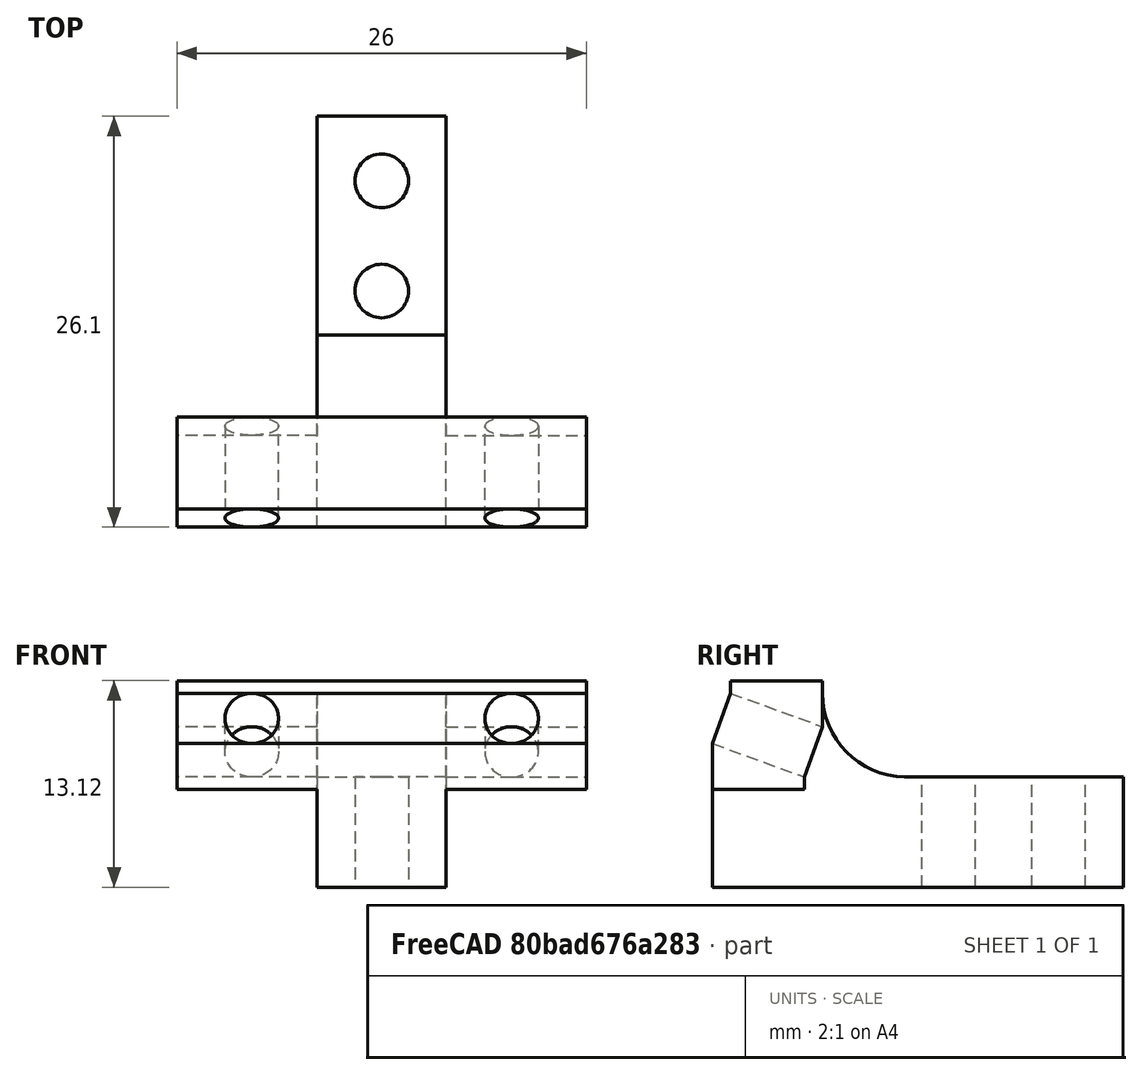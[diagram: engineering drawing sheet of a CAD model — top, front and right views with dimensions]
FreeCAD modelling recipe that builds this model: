
FCSTD DOCUMENT  (FreeCAD 0.19R24291 (Git))
Label: Иголки 70 2
License: All rights reserved
LicenseURL: http://en.wikipedia.org/wiki/All_rights_reserved
objects: PartDesign::Pad×5, Sketcher::SketchObject×4, Mesh::Feature×1, PartDesign::Pocket×1, PartDesign::Mirrored×1, PartDesign::Body×1
note: 18 computed .brp shape members not serialized (recipe doc carries the construction recipe); baked Part::Feature solids carry a one-line shape summary decoded from their .brp

FEATURE [Mesh::Feature] ____________55  label="Иголки55"
FEATURE [Sketcher::SketchObject] Sketch
  FullyConstrained = true
  MapMode = 5
  Support = -> [XY_Plane]
  sketch-geometry (8):
    g0: ArcOfCircle CenterX=0 CenterY=22 CenterZ=0 NormalX=0 NormalY=0 NormalZ=1 AngleXU=0 Radius=1.7 StartAngle=1.5708 EndAngle=4.71239
    g1: ArcOfCircle CenterX=0 CenterY=15 CenterZ=0 NormalX=0 NormalY=0 NormalZ=1 AngleXU=0 Radius=1.7 StartAngle=1.5708 EndAngle=4.71239
    g2: LineSegment StartX=1e-16 StartY=23.7 StartZ=0 EndX=0 EndY=26.1 EndZ=0
    g3: LineSegment StartX=0 StartY=26.1 StartZ=0 EndX=-4.1 EndY=26.1 EndZ=0
    g4: LineSegment StartX=-4.1 StartY=26.1 StartZ=0 EndX=-4.1 EndY=0 EndZ=0
    g5: LineSegment StartX=-4.1 StartY=0 StartZ=0 EndX=0 EndY=0 EndZ=0
    g6: LineSegment StartX=0 StartY=0 StartZ=0 EndX=-3e-16 EndY=13.3 EndZ=0
    g7: LineSegment StartX=1e-16 StartY=16.7 StartZ=0 EndX=-3e-16 EndY=20.3 EndZ=0
  constraints (26):
    c: PointOnObject(g0,g-2)
    c: PointOnObject(g0,g-2)
    c: PointOnObject(g0,g-2)
    c: PointOnObject(g1,g-2)
    c: PointOnObject(g1,g-2)
    c: PointOnObject(g1,g-2)
    c: Diameter(g1) = 3.4
    c: Equal(g1,g0)
    c: Distance(g1,g0) = 7
    c: Coincident(g2,g0)
    c: PointOnObject(g2,g-2)
    c: Distance(g2) = 2.4
    c: Coincident(g3,g2)
    c: Horizontal(g3)
    c: Distance(g1,g-1) = 15
    c: Distance(g3) = 4.1
    c: Coincident(g4,g3)
    c: PointOnObject(g4,g-1)
    c: Vertical(g4)
    c: Coincident(g5,g4)
    c: Coincident(g5,g-1)
    c: Coincident(g6,g5)
    c: Coincident(g6,g1)
    c: Coincident(g7,g1)
    c: Coincident(g7,g0)
    c: Distance(g4) = 26.1
FEATURE [PartDesign::Pad] Pad
  Direction = (1,1,1)
  Length = 7
  Length2 = 100
  Profile = -> Sketch
  Type = 0
FEATURE [Sketcher::SketchObject] Sketch001
  FullyConstrained = true
  MapMode = 5
  Placement = pos=(0,0,0) rot=(0.57735,0.57735,0.57735;2.0944rad)
  Support = -> [YZ_Plane]
  sketch-geometry (11):
    g0: LineSegment StartX=0 StartY=6.999 StartZ=0 EndX=5.83713 EndY=6.999 EndZ=0
    g1: LineSegment StartX=5.83713 StartY=6.999 StartZ=0 EndX=7 EndY=10.194 EndZ=0
    g2: LineSegment StartX=7 StartY=10.194 StartZ=0 EndX=7 EndY=12.3185 EndZ=0
    g3: LineSegment StartX=7 StartY=12.3185 StartZ=0 EndX=1.16287 EndY=12.3185 EndZ=0
    g4: LineSegment StartX=1.16287 StartY=12.3185 StartZ=0 EndX=0 EndY=9.12354 EndZ=0
    g5: LineSegment StartX=0 StartY=9.12354 StartZ=0 EndX=0 EndY=6.999 EndZ=0
    g6: LineSegment StartX=0 StartY=6.999 StartZ=0 EndX=7 EndY=6.999 EndZ=0
    g7: LineSegment StartX=7 StartY=6.999 StartZ=0 EndX=7 EndY=12.3185 EndZ=0
    g8: LineSegment StartX=0 StartY=6.999 StartZ=0 EndX=0 EndY=12.3185 EndZ=0
    g9: LineSegment StartX=0 StartY=12.3185 StartZ=0 EndX=7 EndY=12.3185 EndZ=0
    g10: LineSegment StartX=0 StartY=9.12354 StartZ=0 EndX=5.83713 EndY=6.999 EndZ=0
  constraints (30):
    c: PointOnObject(g0,g-2)
    c: Horizontal(g0)
    c: Coincident(g0,g1)
    c: Coincident(g1,g2)
    c: Vertical(g2)
    c: Coincident(g2,g3)
    c: Horizontal(g3)
    c: Coincident(g3,g4)
    c: PointOnObject(g4,g-2)
    c: Coincident(g4,g5)
    c: Coincident(g5,g0)
    c: Distance(g-1,g0) = 6.999
    c: Equal(g0,g3)
    c: Equal(g2,g5)
    c: DistanceX(g2) = 7
    c: Coincident(g6,g0)
    c: Horizontal(g6)
    c: Coincident(g7,g6)
    c: Coincident(g7,g2)
    c: Vertical(g7)
    c: Coincident(g8,g0)
    c: PointOnObject(g8,g-2)
    c: Coincident(g9,g8)
    c: Coincident(g9,g2)
    c: Horizontal(g9)
    c: Distance(g1) = 3.4
    c: Angle(g1,g6) = 1.91986
    c: Coincident(g10,g4)
    c: Coincident(g10,g0)
    c: Perpendicular(g10,g1)
FEATURE [PartDesign::Pad] Pad001
  BaseFeature = -> Pad
  Direction = (1,1,1)
  Length = 13
  Length2 = 100
  Profile = -> Sketch001
  Reversed = true
  Type = 0
FEATURE [Sketcher::SketchObject] Sketch002
  FullyConstrained = true
  MapMode = 5
  Placement = pos=(0,0,0) rot=(0.57735,0.57735,0.57735;2.0944rad)
  Support = -> [YZ_Plane]
  expr: Constraints[11] = Sketch001.Constraints[11]
  expr: Constraints[14] = Sketch001.Constraints[14]
  expr: Constraints[25] = Sketch001.Constraints[25]
  expr: Constraints[26] = Sketch001.Constraints[26]
  sketch-geometry (13):
    g0: LineSegment StartX=0 StartY=6.999 StartZ=0 EndX=5.83713 EndY=6.999 EndZ=0
    g1: LineSegment StartX=5.83713 StartY=6.999 StartZ=0 EndX=7 EndY=10.194 EndZ=0
    g2: LineSegment StartX=7 StartY=10.194 StartZ=0 EndX=7 EndY=12.3185 EndZ=0
    g3: LineSegment StartX=7 StartY=12.3185 StartZ=0 EndX=1.16287 EndY=12.3185 EndZ=0
    g4: LineSegment StartX=1.16287 StartY=12.3185 StartZ=0 EndX=0 EndY=9.12354 EndZ=0
    g5: LineSegment StartX=0 StartY=9.12354 StartZ=0 EndX=0 EndY=6.999 EndZ=0
    g6: LineSegment StartX=0 StartY=6.999 StartZ=0 EndX=7 EndY=6.999 EndZ=0
    g7: LineSegment StartX=7 StartY=6.999 StartZ=0 EndX=7 EndY=12.3185 EndZ=0
    g8: LineSegment StartX=0 StartY=6.999 StartZ=0 EndX=0 EndY=12.3185 EndZ=0
    g9: LineSegment StartX=0 StartY=12.3185 StartZ=0 EndX=7 EndY=12.3185 EndZ=0
    g10: LineSegment StartX=0 StartY=9.12354 StartZ=0 EndX=5.83713 EndY=6.999 EndZ=0
    g11: ArcOfCircle CenterX=12.3195 CenterY=12.3185 CenterZ=0 NormalX=0 NormalY=0 NormalZ=1 AngleXU=0 Radius=5.31949 StartAngle=3.14159 EndAngle=4.71239
    g12: LineSegment StartX=5.83713 StartY=6.999 StartZ=0 EndX=12.3195 EndY=6.999 EndZ=0
  constraints (36):
    c: PointOnObject(g0,g-2)
    c: Horizontal(g0)
    c: Coincident(g0,g1)
    c: Coincident(g1,g2)
    c: Vertical(g2)
    c: Coincident(g2,g3)
    c: Horizontal(g3)
    c: Coincident(g3,g4)
    c: PointOnObject(g4,g-2)
    c: Coincident(g4,g5)
    c: Coincident(g5,g0)
    c: Distance(g-1,g0) = 6.999
    c: Equal(g0,g3)
    c: Equal(g2,g5)
    c: DistanceX(g2) = 7
    c: Coincident(g6,g0)
    c: Horizontal(g6)
    c: Coincident(g7,g6)
    c: Coincident(g7,g2)
    c: Vertical(g7)
    c: Coincident(g8,g0)
    c: PointOnObject(g8,g-2)
    c: Coincident(g9,g8)
    c: Coincident(g9,g2)
    c: Horizontal(g9)
    c: Distance(g1) = 3.4
    c: Angle(g1,g6) = 1.91986
    c: Coincident(g10,g4)
    c: Coincident(g10,g0)
    c: Perpendicular(g10,g1)
    c: Coincident(g11,g2)
    c: Tangent(g11,g2)
    c: Coincident(g12,g1)
    c: Coincident(g12,g11)
    c: Horizontal(g12)
    c: Tangent(g12,g11)
FEATURE [PartDesign::Pad] Pad002
  BaseFeature = -> Pad001
  Direction = (1,1,1)
  Length = 4.1
  Length2 = 100
  Profile = -> Sketch002
  Reversed = true
  Type = 0
FEATURE [Sketcher::SketchObject] Sketch003
  ExternalGeometry = -> [Pad002]
  FullyConstrained = true
  MapMode = 5
  Placement = pos=(9e-16,2.90488,-1.05729) rot=(0,0.819152,0.573576;3.14159rad)
  Support = -> [Pad002]
  sketch-geometry (1):
    g0: Circle CenterX=8.25 CenterY=10.2733 CenterZ=0 NormalX=0 NormalY=0 NormalZ=1 AngleXU=0 Radius=1.7
  constraints (3):
    c: Tangent(g0,g-4)
    c: Tangent(g0,g-3)
    c: Distance(g0,g-2) = 8.25
FEATURE [PartDesign::Pocket] Pocket
  BaseFeature = -> Pad002
  Length = 5
  Length2 = 100
  Profile = -> Sketch003
  Type = 1
FEATURE [PartDesign::Pad] Pad003
  BaseFeature = -> Pocket
  Direction = (1,1,1)
  Length = 0.8
  Length2 = 100
  Profile = -> Pocket [Face19]
  Type = 0
FEATURE [PartDesign::Pad] Pad004
  BaseFeature = -> Pad003
  Direction = (1,1,1)
  Length = 0.8
  Length2 = 100
  Profile = -> Pad003 [Face12]
  Type = 0
FEATURE [PartDesign::Mirrored] Mirrored
  BaseFeature = -> Pad004
  MirrorPlane = -> Sketch [V_Axis]
  Originals = -> [Pad,Pad001,Pad002,Pocket,Pad003,Pad004]
FEATURE [PartDesign::Body] Body
  Group = -> [Sketch,Pad,Sketch001,Pad001,Sketch002,Pad002,Sketch003,Pocket,Pad003,Pad004,Mirrored]
  Origin = -> Origin
  Tip = -> Mirrored
